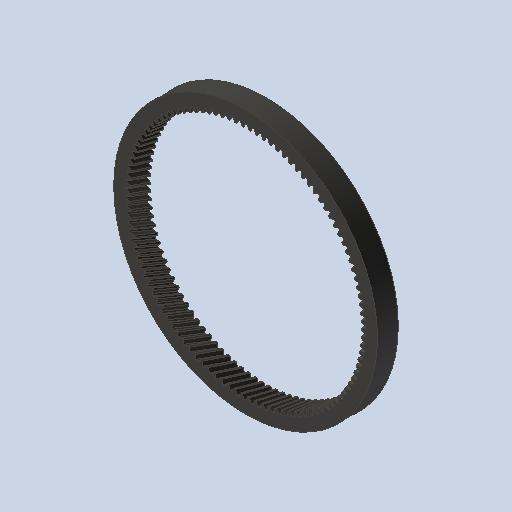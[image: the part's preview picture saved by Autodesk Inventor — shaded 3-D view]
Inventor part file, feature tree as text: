
AUTODESK INVENTOR PART (.ipt)
format: ipt  version: 2023 (Build 270158000, 158)  size: 1,273,856 bytes
history: native  units: mm (DEFAULTED — no unit token found)
features: plane x3, other x3, sketch x2, extrude x1
ambient origin geometry x8: Origin, YZ Plane, XZ Plane, XY Plane, X Axis, Y Axis, Z Axis, Center Point
bodies: Solid1 (feature_tree)
feature tree (9):
  extrude  "Extrusion1"  Depth=10.0mm TaperAngle=0.0deg
  plane  "Work Plane2"
  plane  "Work Plane8"
  plane  "Work Plane9"
  other  "Spur Gear"
  sketch  "Sketch1"  dims[d0=126.797186mm d1=10.0mm d2=0.0mm]
  sketch  "Sketch2"  dims[d3=112.802844mm d4=10.0mm d5=0.0mm d16=50.0mm d17=0.0mm d34=0.296377mm d39=0.0mm d45=0.0mm d47=50.0mm d50=0.0mm d51=0.0mm d52=50.0mm]
  other  "Srf1"
  other  "Pitch Diameter"
